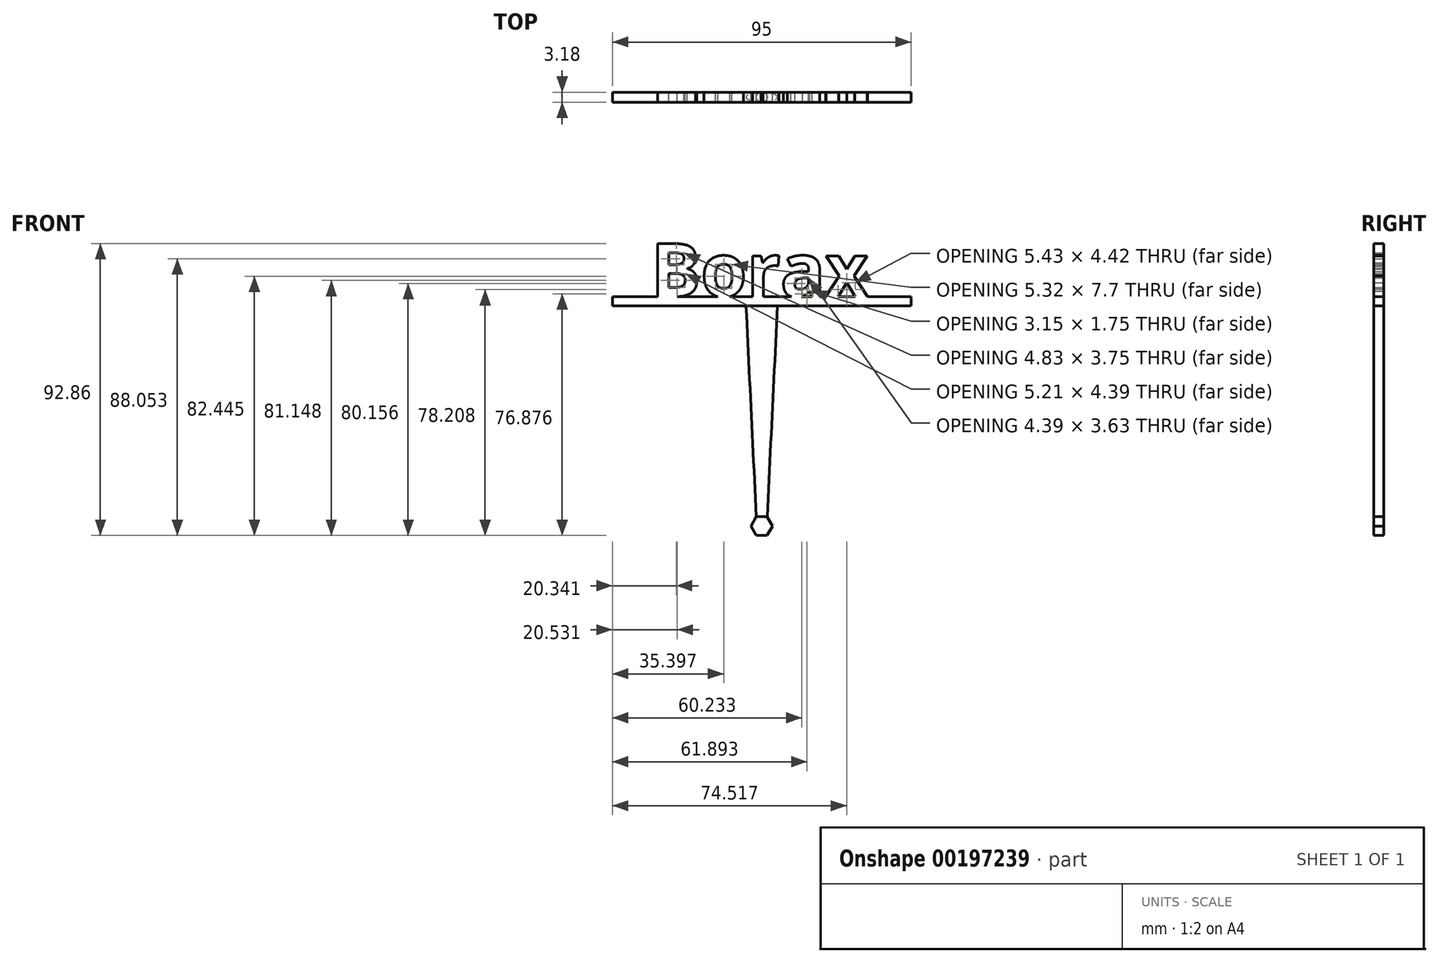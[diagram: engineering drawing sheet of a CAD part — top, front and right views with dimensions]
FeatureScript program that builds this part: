
annotation { "Feature Type Name" : "Feature", "Feature Type Description" : "" }
export const myFeature = defineFeature(function(context is Context, id is Id, definition is map)
    precondition{}
    {
        {
            var Q0;
            Q0=qCreatedBy(makeId("Front.planeOp"),FACE);
            var sketch = newSketch(context, id + "F0", { "sketchPlane" : qUnion([Q0])});
            skLineSegment(sketch, "E0.bottom", {"start": v(-47.5, 3) * mm, "end": v(47.5, 3) * mm});
            skLineSegment(sketch, "E0.top", {"start": v(-47.5, 0) * mm, "end": v(47.5, 0) * mm});
            skLineSegment(sketch, "E0.left", {"start": v(-47.5, 3) * mm, "end": v(-47.5, 0) * mm});
            skLineSegment(sketch, "E0.right", {"start": v(47.5, 3) * mm, "end": v(47.5, 0) * mm});
            skText(sketch, "E1", { "text": "Borax", "fontName": "OpenSans-Bold.ttf"});
            const initialGuessF0  = {"E1": [-0.03527, 0.003, 1, 0, 0.017]};
            skSetInitialGuess(sketch, initialGuessF0);
            skSolve(sketch);
        }
        {
            var Q0;
            Q0=qSketchRegion(id+"F0",true);
            extrude(context, id + "F1", {"entities" : qUnion([Q0]), "depth" : 3.17 * mm});
        }
        {
            var Q0;
            Q0=qCreatedBy(makeId("Top.planeOp"),FACE);
            var sketch = newSketch(context, id + "F2", { "sketchPlane" : qUnion([Q0])});
            skLineSegment(sketch, "E2.bottom", {"start": v(0, 0) * mm, "end": v(2.5, 0) * mm, "construction": true});
            skLineSegment(sketch, "E2.top", {"start": v(0, -3.17) * mm, "end": v(2.5, -3.17) * mm, "construction": true});
            skLineSegment(sketch, "E2.left", {"start": v(0, 0) * mm, "end": v(0, -3.18) * mm, "construction": true});
            skLineSegment(sketch, "E2.right", {"start": v(2.5, 0) * mm, "end": v(2.5, -3.17) * mm, "construction": true});
            skEllipse(sketch, "E3", {"center": v(0, -1.59) * mm, "majorRadius": 5 * mm, "minorRadius": 1.59 * mm, "majorAxis": v(1, 0)});
            skSolve(sketch);
        }
        {
            var Q0;
            Q0=qCreatedBy(makeId("Top.planeOp"),FACE);
            cPlane(context, id + "F3", {"entities" : qUnion([Q0]), "cplaneType" : CPlaneType.OFFSET, "offset" : 70 * mm, "oppositeDirection" : true, "width" : 150 * mm, "height" : 150 * mm});
        }
        {
            var Q0;
            Q0=qCreatedBy(id+"F3.planeOp",FACE);
            var sketch = newSketch(context, id + "F4", { "sketchPlane" : qUnion([Q0])});
            skPoint(sketch, "E4", {"position": v(0, 0) * mm});
            skLineSegment(sketch, "E5.0", {"start": v(-50.9, -1.59) * mm, "end": v(49.1, -1.59) * mm, "construction": true});
            skLineSegment(sketch, "E6.0", {"start": v(0, 0) * mm, "end": v(0, -3.17) * mm, "construction": true});
            skCircle(sketch, "E7", {"center": v(0, -1.59) * mm, "radius": 1.59 * mm});
            skSolve(sketch);
        }
        {
            var Q1;
            Q1=makeQuery(id+"F2.imprint","IMPRINT",FACE,{"disambiguationData":[TD([[makeQuery(id+"F2.imprint","IMPRINT",EDGE,{"derivedFrom":sQuery(id+"F2.wireOp",EDGE,"E3")}),1.0]])]});
            var Q2;
            Q2=makeQuery(id+"F4.imprint","IMPRINT",FACE,{"disambiguationData":[TD([[makeQuery(id+"F4.imprint","IMPRINT",EDGE,{"derivedFrom":sQuery(id+"F4.wireOp",EDGE,"E7")}),1.0]])]});
            loft(context, id + "F5", {"operationType" : NewBodyOperationType.ADD, "sheetProfilesArray" : [{ "sheetProfileEntities" : qUnion([Q1]) }, { "sheetProfileEntities" : qUnion([Q2]) }]});
        }
        {
            var Q0;
            Q0=qCreatedBy(makeId("Front.planeOp"),FACE);
            var sketch = newSketch(context, id + "F6", { "sketchPlane" : qUnion([Q0])});
            skLineSegment(sketch, "E8.bottom", {"start": v(3, -73) * mm, "end": v(-3, -73) * mm, "construction": true});
            skLineSegment(sketch, "E8.top", {"start": v(3, -67) * mm, "end": v(-3, -67) * mm, "construction": true});
            skLineSegment(sketch, "E8.left", {"start": v(3, -73) * mm, "end": v(3, -67) * mm, "construction": true});
            skLineSegment(sketch, "E8.right", {"start": v(-3, -73) * mm, "end": v(-3, -67) * mm, "construction": true});
            skPoint(sketch, "E8.middle", {"position": v(0, -70) * mm});
            skCircle(sketch, "E9.cCircle", {"center": v(0, -70) * mm, "radius": 3 * mm, "construction": true});
            skLineSegment(sketch, "E9.0", {"start": v(0, -73) * mm, "end": v(-2.6, -71.5) * mm, "construction": true});
            skLineSegment(sketch, "E9.1", {"start": v(-2.6, -71.5) * mm, "end": v(-2.6, -68.5) * mm, "construction": true});
            skLineSegment(sketch, "E9.2", {"start": v(-2.6, -68.5) * mm, "end": v(0, -67) * mm, "construction": true});
            skLineSegment(sketch, "E9.3", {"start": v(0, -67) * mm, "end": v(2.6, -68.5) * mm, "construction": true});
            skLineSegment(sketch, "E9.4", {"start": v(2.6, -68.5) * mm, "end": v(2.6, -71.5) * mm, "construction": true});
            skLineSegment(sketch, "E9.5", {"start": v(2.6, -71.5) * mm, "end": v(0, -73) * mm, "construction": true});
            skLineSegment(sketch, "E10.0", {"start": v(1.73, -73) * mm, "end": v(-1.73, -73) * mm});
            skLineSegment(sketch, "E10.1", {"start": v(-1.73, -73) * mm, "end": v(-3.46, -70) * mm});
            skLineSegment(sketch, "E10.2", {"start": v(-3.46, -70) * mm, "end": v(-1.73, -67) * mm});
            skLineSegment(sketch, "E10.3", {"start": v(-1.73, -67) * mm, "end": v(1.73, -67) * mm});
            skLineSegment(sketch, "E10.4", {"start": v(1.73, -67) * mm, "end": v(3.46, -70) * mm});
            skLineSegment(sketch, "E10.5", {"start": v(3.46, -70) * mm, "end": v(1.73, -73) * mm});
            skPoint(sketch, "E10.0.midPoint", {"position": v(0, -73) * mm});
            skSolve(sketch);
        }
        {
            var Q0;
            Q0=makeQuery(id+"F6.imprint","IMPRINT",FACE,{"disambiguationData":[TD([[makeQuery(id+"F6.imprint","IMPRINT",EDGE,{"derivedFrom":sQuery(id+"F6.wireOp",EDGE,"E10.0")}),-1.0]])]});
            extrude(context, id + "F7", {"entities" : qUnion([Q0]), "operationType" : NewBodyOperationType.ADD, "depth" : 3.17 * mm});
        }
    });
